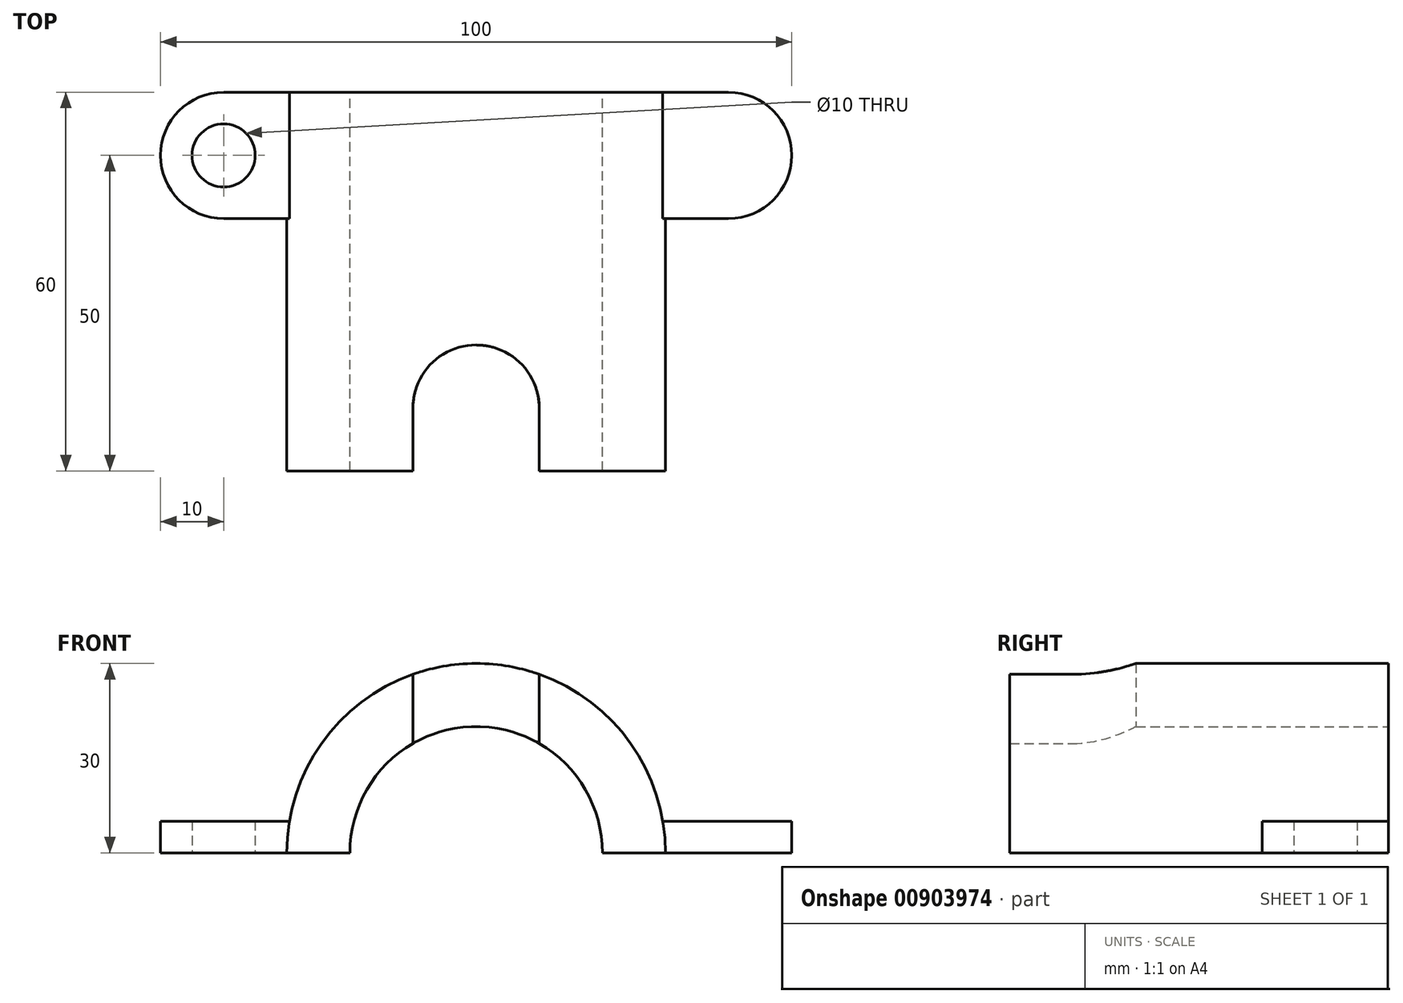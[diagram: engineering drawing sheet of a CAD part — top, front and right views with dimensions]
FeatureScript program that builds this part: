
annotation { "Feature Type Name" : "Feature", "Feature Type Description" : "" }
export const myFeature = defineFeature(function(context is Context, id is Id, definition is map)
    precondition{}
    {
        {
            var Q0;
            Q0=qCreatedBy(makeId("Front.planeOp"),FACE);
            var sketch = newSketch(context, id + "F0", { "sketchPlane" : qUnion([Q0])});
            skArc(sketch, "E0", {"start": v(30, 0) * mm, "mid": v(0, 30) * mm, "end": v(-30, 0) * mm});
            skLineSegment(sketch, "E1", {"start": v(-30, 0) * mm, "end": v(30, 0) * mm});
            skSolve(sketch);
        }
        {
            var Q0;
            Q0=makeQuery(id+"F0.imprint","IMPRINT",FACE,{"disambiguationData":[TD([[makeQuery(id+"F0.imprint","IMPRINT",EDGE,{"derivedFrom":sQuery(id+"F0.wireOp",EDGE,"E0")}),1.0]])]});
            extrude(context, id + "F1", {"entities" : qUnion([Q0]), "depth" : 60 * mm, "offsetDistance" : 25 * mm});
        }
        {
            var Q0;
            Q0=qCreatedBy(makeId("Top.planeOp"),FACE);
            var sketch = newSketch(context, id + "F2", { "sketchPlane" : qUnion([Q0])});
            skLineSegment(sketch, "E2.bottom", {"start": v(-40, 0) * mm, "end": v(40, 0) * mm});
            skLineSegment(sketch, "E2.top", {"start": v(-40, -20) * mm, "end": v(40, -20) * mm});
            skLineSegment(sketch, "E3.0", {"start": v(-40, -10) * mm, "end": v(40, -10) * mm, "construction": true});
            skArc(sketch, "E4", {"start": v(-40, 0) * mm, "mid": v(-50, -10) * mm, "end": v(-40, -20) * mm});
            skArc(sketch, "E5.MirrorCS", {"start": v(40, 0) * mm, "mid": v(50, -10) * mm, "end": v(40, -20) * mm});
            skSolve(sketch);
        }
        {
            var Q0;
            Q0=makeQuery(id+"F2.imprint","IMPRINT",FACE,{"disambiguationData":[TD([[makeQuery(id+"F2.imprint","IMPRINT",EDGE,{"derivedFrom":sQuery(id+"F2.wireOp",EDGE,"E2.bottom")}),-1.0]])]});
            extrude(context, id + "F3", {"entities" : qUnion([Q0]), "operationType" : NewBodyOperationType.ADD, "depth" : 5 * mm, "offsetDistance" : 25 * mm});
        }
        {
            var Q0;
            Q0=qCreatedBy(makeId("Top.planeOp"),FACE);
            var sketch = newSketch(context, id + "F4", { "sketchPlane" : qUnion([Q0])});
            skCircle(sketch, "E6", {"center": v(-40, -10) * mm, "radius": 5 * mm});
            skCircle(sketch, "E7.MirrorC", {"center": v(40, -10) * mm, "radius": 5 * mm});
            skSolve(sketch);
        }
        {
            var Q0;
            Q0=makeQuery(id+"F4.imprint","IMPRINT",FACE,{"disambiguationData":[TD([[makeQuery(id+"F4.imprint","IMPRINT",EDGE,{"derivedFrom":sQuery(id+"F4.wireOp",EDGE,"E6")}),1.0]])]});
            var Q1;
            Q1=makeQuery(id+"F4.imprint","IMPRINT",FACE,{"disambiguationData":[TD([[makeQuery(id+"F4.imprint","IMPRINT",EDGE,{"derivedFrom":sQuery(id+"F4.wireOp",EDGE,"E7.MirrorC")}),-1.0]])]});
            extrude(context, id + "F5", {"entities" : qUnion([Q0, Q1]), "operationType" : NewBodyOperationType.REMOVE, "endBound" : BoundingType.THROUGH_ALL, "depth" : 25 * mm, "offsetDistance" : 25 * mm});
        }
        {
            var Q0;
            Q0=qCreatedBy(makeId("Top.planeOp"),FACE);
            var sketch = newSketch(context, id + "F6", { "sketchPlane" : qUnion([Q0])});
            skLineSegment(sketch, "E8.bottom", {"start": v(10, -60.04) * mm, "end": v(-10, -60.04) * mm});
            skLineSegment(sketch, "E8.top", {"start": v(10, -40.04) * mm, "end": v(-10, -40.04) * mm});
            skLineSegment(sketch, "E8.left", {"start": v(10, -60.04) * mm, "end": v(10, -40.04) * mm});
            skLineSegment(sketch, "E8.right", {"start": v(-10, -60.04) * mm, "end": v(-10, -40.04) * mm});
            skSolve(sketch);
        }
        {
            var Q0;
            Q0=makeQuery(id+"F6.imprint","IMPRINT",FACE,{"disambiguationData":[TD([[makeQuery(id+"F6.imprint","IMPRINT",EDGE,{"derivedFrom":sQuery(id+"F6.wireOp",EDGE,"E8.bottom")}),-1.0]])]});
            extrude(context, id + "F7", {"entities" : qUnion([Q0]), "operationType" : NewBodyOperationType.REMOVE, "endBound" : BoundingType.THROUGH_ALL, "depth" : 25 * mm, "offsetDistance" : 25 * mm});
        }
        {
            var Q0;
            Q0=makeQuery(id+"F7.boolean.opBoolean","COPY",EDGE,{"derivedFrom":makeQuery(id+"F7.opExtrude","SWEPT_EDGE",EDGE,{"disambiguationData":[OSD([sQuery(id+"F6.wireOp",EDGE,"E8.top"),sQuery(id+"F6.wireOp",EDGE,"E8.right")])]})});
            var Q1;
            Q1=makeQuery(id+"F7.boolean.opBoolean","COPY",EDGE,{"derivedFrom":makeQuery(id+"F7.opExtrude","SWEPT_EDGE",EDGE,{"disambiguationData":[OSD([sQuery(id+"F6.wireOp",EDGE,"E8.top"),sQuery(id+"F6.wireOp",EDGE,"E8.left")])]})});
            fillet(context, id + "F8", {"entities" : qUnion([Q0, Q1]), "radius" : 10 * mm, "tangentPropagation" : true, "allowEdgeOverflow" : false});
        }
        {
            var Q0;
            Q0=makeQuery(id+"F3.boolean.opBoolean","MERGE",FACE,{"derivedFrom":[makeQuery(id+"F1.opExtrude","CAP_FACE",FACE,{"disambiguationData":[OSD([sQuery(id+"F0.wireOp",EDGE,"E0"),sQuery(id+"F0.wireOp",EDGE,"E1")])],"isStart":true}),makeQuery(id+"F3.opExtrude","SWEPT_FACE",FACE,{"disambiguationData":[OSD([sQuery(id+"F2.wireOp",EDGE,"E2.bottom")])]})]});
            var sketch = newSketch(context, id + "F9", { "sketchPlane" : qUnion([Q0])});
            skArc(sketch, "E9", {"start": v(20, 0) * mm, "mid": v(0, 20) * mm, "end": v(-20, 0) * mm});
            skLineSegment(sketch, "E10", {"start": v(-20, 0) * mm, "end": v(20, 0) * mm});
            skSolve(sketch);
        }
        {
            var Q0;
            Q0=makeQuery(id+"F9.imprint","IMPRINT",FACE,{"disambiguationData":[TD([[makeQuery(id+"F9.imprint","IMPRINT",EDGE,{"derivedFrom":sQuery(id+"F9.wireOp",EDGE,"E9")}),1.0]])]});
            extrude(context, id + "F10", {"entities" : qUnion([Q0]), "operationType" : NewBodyOperationType.REMOVE, "endBound" : BoundingType.THROUGH_ALL, "oppositeDirection" : true, "depth" : 25 * mm, "offsetDistance" : 25 * mm});
        }
    });
